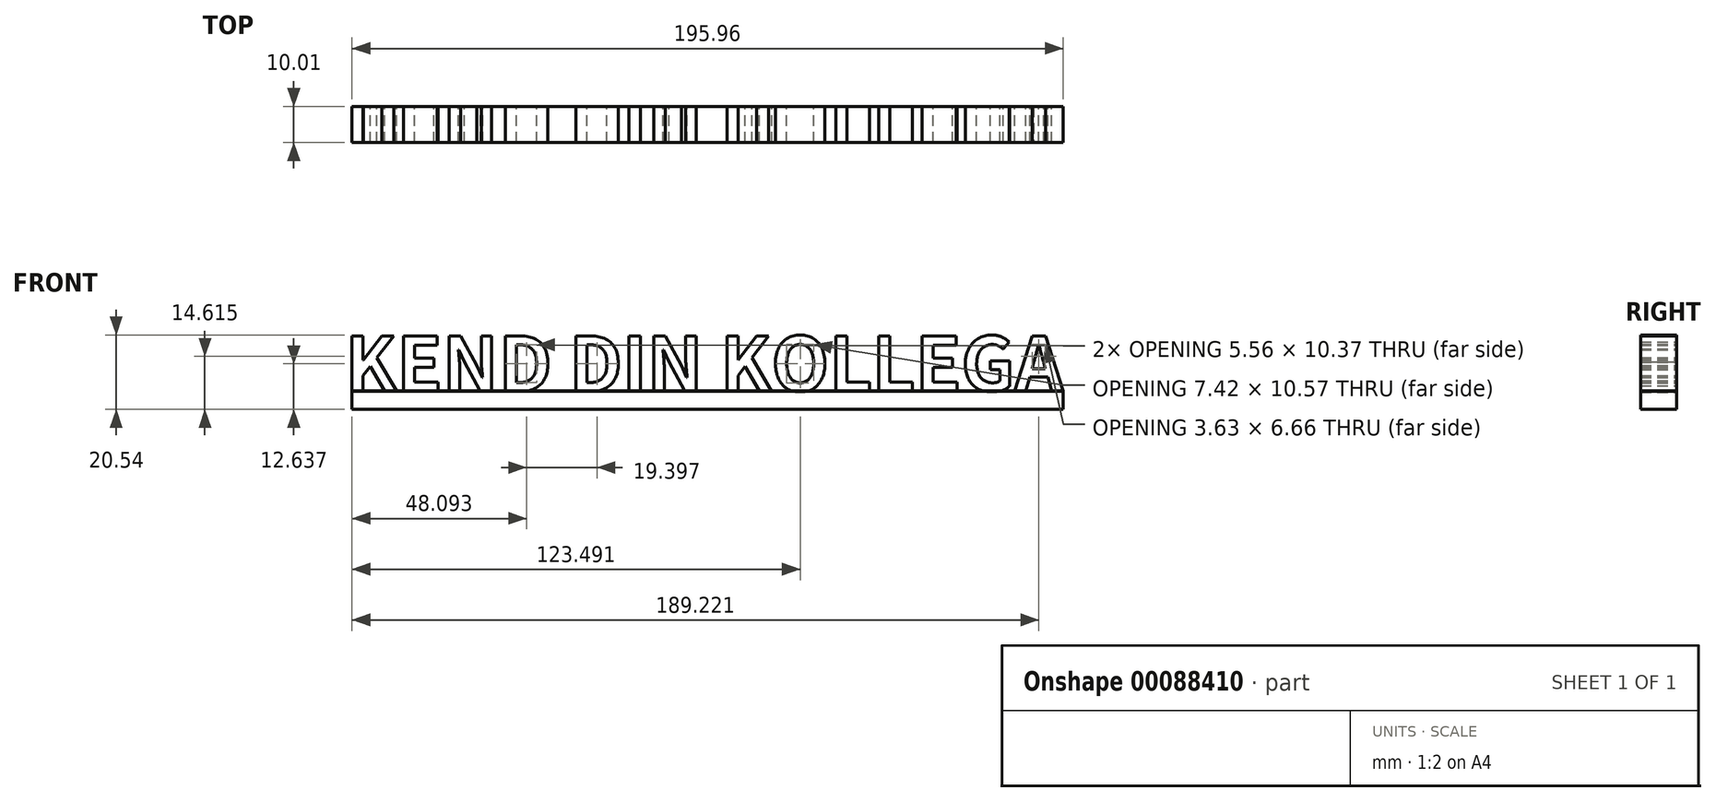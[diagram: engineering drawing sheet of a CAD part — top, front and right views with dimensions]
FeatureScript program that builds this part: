
annotation { "Feature Type Name" : "Feature", "Feature Type Description" : "" }
export const myFeature = defineFeature(function(context is Context, id is Id, definition is map)
    precondition{}
    {
        {
            var Q0;
            Q0=qCreatedBy(makeId("Front.planeOp"),FACE);
            var sketch = newSketch(context, id + "F0", { "sketchPlane" : qUnion([Q0])});
            skText(sketch, "E0", { "text": "KEND DIN KOLLEGA", "fontName": "NotoSansCJKsc-Bold.otf"});
            const initialGuessF0  = {"E0": [-0.05423, 0, 1, 0, 0.01484]};
            skSetInitialGuess(sketch, initialGuessF0);
            skSolve(sketch);
        }
        {
            var Q0;
            Q0 = qSketchRegion(id + "F0", true);
            extrude(context, id + "F1", {"entities" : qUnion([Q0]), "depth" : 10 * mm});
        }
        {
            var Q0;
            Q0=qCreatedBy(makeId("Top.planeOp"),FACE);
            var sketch = newSketch(context, id + "F2", { "sketchPlane" : qUnion([Q0])});
            skLineSegment(sketch, "E1.bottom", {"start": v(-52.36, 0) * mm, "end": v(143.58, 0) * mm});
            skLineSegment(sketch, "E1.top", {"start": v(-52.36, -10) * mm, "end": v(143.58, -10) * mm});
            skLineSegment(sketch, "E1.left", {"start": v(-52.36, 0) * mm, "end": v(-52.36, -10) * mm});
            skLineSegment(sketch, "E1.right", {"start": v(143.58, 0) * mm, "end": v(143.58, -10) * mm});
            skSolve(sketch);
        }
        {
            var Q0;
            Q0=makeQuery(id+"F2.imprint","IMPRINT",FACE,{"disambiguationData":[TD([[makeQuery(id+"F2.imprint","IMPRINT",EDGE,{"derivedFrom":sQuery(id+"F2.wireOp",EDGE,"E1.bottom")}),-1.0]])]});
            extrude(context, id + "F3", {"entities" : qUnion([Q0]), "oppositeDirection" : true, "depth" : 5 * mm});
        }
        {
            var Q0;
            Q0=makeQuery(id+"F2.imprint","IMPRINT",FACE,{"disambiguationData":[TD([[makeQuery(id+"F2.imprint","IMPRINT",EDGE,{"derivedFrom":sQuery(id+"F2.wireOp",EDGE,"E1.bottom")}),-1.0]])]});
            extrude(context, id + "F4", {"entities" : qUnion([Q0]), "depth" : 0.1 * mm});
        }
    });
